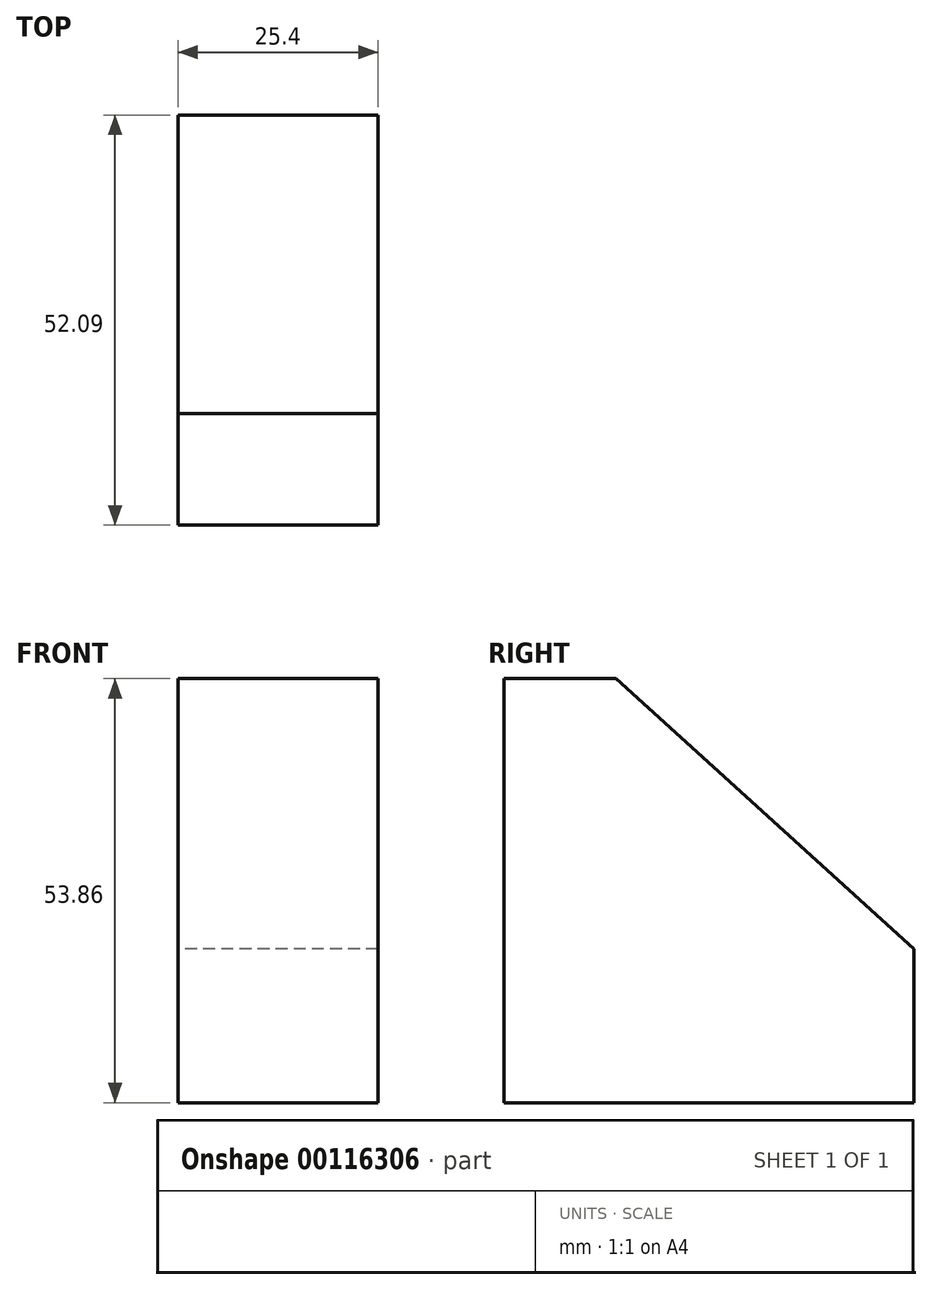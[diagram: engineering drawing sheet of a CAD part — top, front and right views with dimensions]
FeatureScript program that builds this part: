
annotation { "Feature Type Name" : "Feature", "Feature Type Description" : "" }
export const myFeature = defineFeature(function(context is Context, id is Id, definition is map)
    precondition{}
    {
        {
            var Q0;
            Q0=qCreatedBy(makeId("Right.planeOp"),FACE);
            var sketch = newSketch(context, id + "F0", { "sketchPlane" : qUnion([Q0])});
            skLineSegment(sketch, "E0", {"start": v(36.35, -13.08) * mm, "end": v(36.35, 6.43) * mm});
            skLineSegment(sketch, "E1", {"start": v(36.35, 6.43) * mm, "end": v(-1.55, 40.78) * mm});
            skLineSegment(sketch, "E2", {"start": v(-1.55, 40.78) * mm, "end": v(-15.74, 40.78) * mm});
            skLineSegment(sketch, "E3", {"start": v(-15.74, 40.78) * mm, "end": v(-15.74, -13.08) * mm});
            skLineSegment(sketch, "E4", {"start": v(-15.74, -13.08) * mm, "end": v(36.35, -13.08) * mm});
            skSolve(sketch);
        }
        {
            var Q0;
            Q0 = qSketchRegion(id + "F0", true);
            extrude(context, id + "F1", {"entities" : qUnion([Q0]), "depth" : 25.4 * mm});
        }
    });
